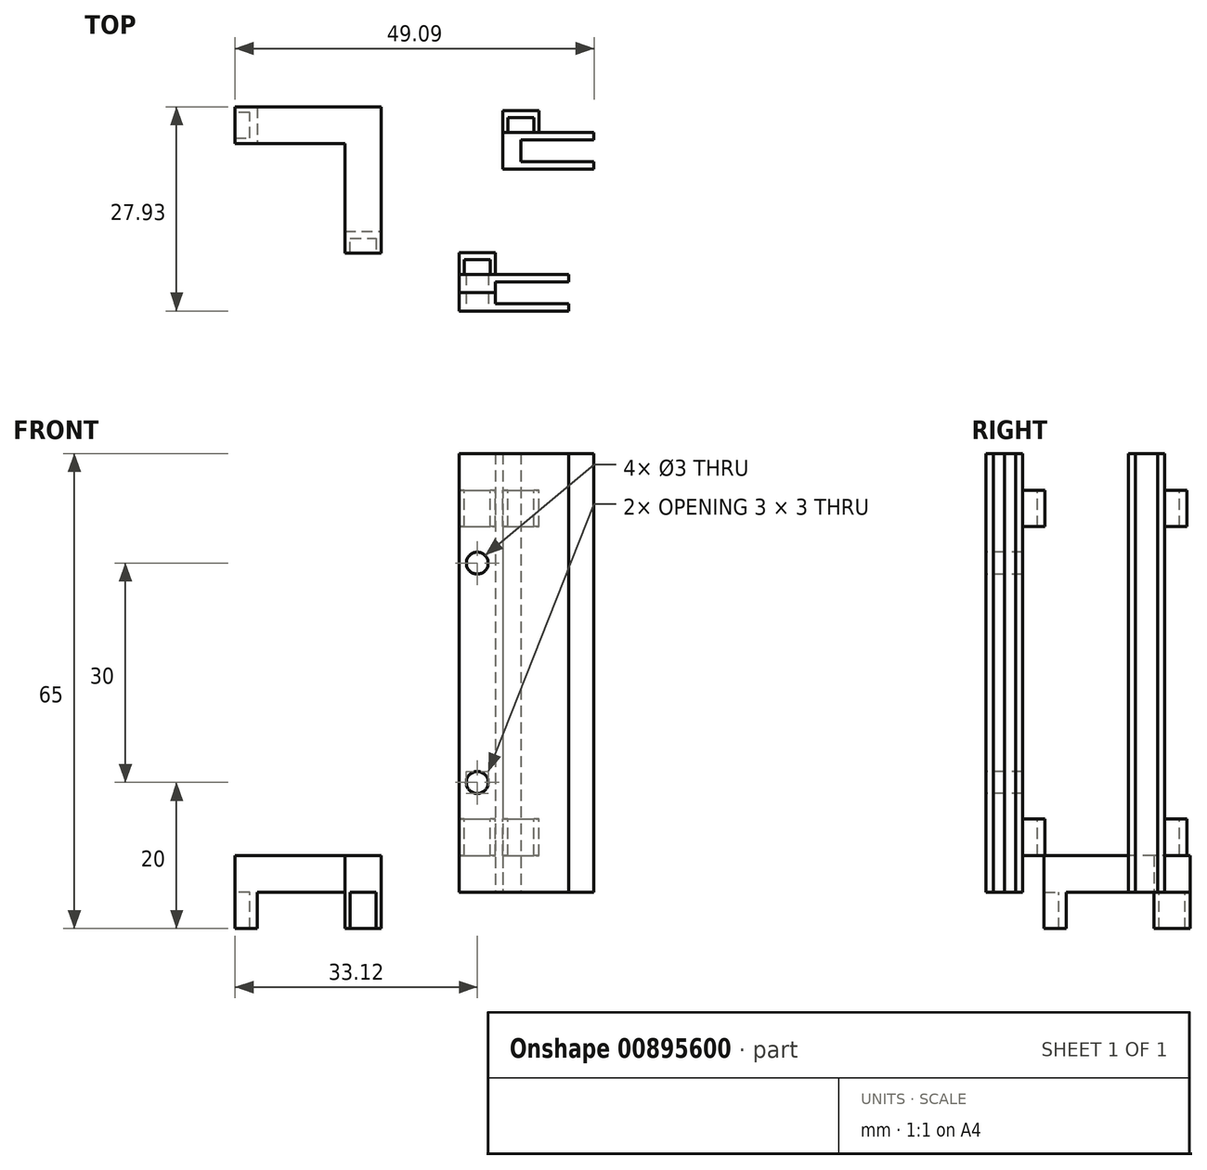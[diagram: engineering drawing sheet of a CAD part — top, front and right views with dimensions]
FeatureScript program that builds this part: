
annotation { "Feature Type Name" : "Feature", "Feature Type Description" : "" }
export const myFeature = defineFeature(function(context is Context, id is Id, definition is map)
    precondition{}
    {
        {
            var Q0;
            Q0=qCreatedBy(makeId("Top.planeOp"),FACE);
            var sketch = newSketch(context, id + "F0", { "sketchPlane" : qUnion([Q0])});
            skLineSegment(sketch, "E0.bottom", {"start": v(0, 0) * mm, "end": v(-10, 0) * mm});
            skLineSegment(sketch, "E0.top", {"start": v(0, 3) * mm, "end": v(-10, 3) * mm});
            skLineSegment(sketch, "E0.left", {"start": v(0, 0) * mm, "end": v(0, 3) * mm});
            skLineSegment(sketch, "E0.right", {"start": v(-10, 0) * mm, "end": v(-10, 3) * mm});
            skLineSegment(sketch, "E1.bottom", {"start": v(0, 0) * mm, "end": v(-15, 0) * mm});
            skLineSegment(sketch, "E1.top", {"start": v(0, -1) * mm, "end": v(-15, -1) * mm});
            skLineSegment(sketch, "E1.left", {"start": v(0, 0) * mm, "end": v(0, -1) * mm});
            skLineSegment(sketch, "E1.right", {"start": v(-15, 0) * mm, "end": v(-15, -1) * mm});
            skLineSegment(sketch, "E2.bottom", {"start": v(0, 3) * mm, "end": v(-15, 3) * mm});
            skLineSegment(sketch, "E2.top", {"start": v(0, 4) * mm, "end": v(-15, 4) * mm});
            skLineSegment(sketch, "E2.left", {"start": v(0, 3) * mm, "end": v(0, 4) * mm});
            skLineSegment(sketch, "E2.right", {"start": v(-15, 3) * mm, "end": v(-15, 4) * mm});
            skLineSegment(sketch, "E3", {"start": v(-15, 3) * mm, "end": v(-15, 0) * mm});
            skLineSegment(sketch, "E4", {"start": v(-15, 1.5) * mm, "end": v(-10, 1.5) * mm});
            skSolve(sketch);
        }
        {
            var Q0;
            Q0=makeQuery(id+"F0.imprint","IMPRINT",FACE,{"disambiguationData":[TD([[makeQuery(id+"F0.imprint","IMPRINT",EDGE,{"derivedFrom":sQuery(id+"F0.wireOp",EDGE,"E2.top")}),1.0]])]});
            var Q1;
            {var subQ3=sQuery(id+"F0.wireOp",EDGE,"E4");Q1=makeQuery(id+"F0.imprint","IMPRINT",FACE,{"disambiguationData":[TD([[makeQuery(id+"F0.imprint","IMPRINT",EDGE,{"derivedFrom":subQ3}),1.0]])]});}
            extrude(context, id + "F1", {"entities" : qUnion([Q0, Q1]), "depth" : 60 * mm});
        }
        {
            var Q0;
            {var subQ3=sQuery(id+"F0.wireOp",EDGE,"E4");Q0=makeQuery(id+"F0.imprint","IMPRINT",FACE,{"disambiguationData":[TD([[makeQuery(id+"F0.imprint","IMPRINT",EDGE,{"derivedFrom":subQ3}),-1.0]])]});}
            var Q1;
            Q1=makeQuery(id+"F0.imprint","IMPRINT",FACE,{"disambiguationData":[TD([[makeQuery(id+"F0.imprint","IMPRINT",EDGE,{"derivedFrom":sQuery(id+"F0.wireOp",EDGE,"E1.top")}),-1.0]])]});
            extrude(context, id + "F2", {"entities" : qUnion([Q0, Q1]), "depth" : 60 * mm});
        }
        {
            var Q0;
            Q0=makeQuery(id+"F2.opExtrude","SWEPT_FACE",FACE,{"disambiguationData":[OSD([sQuery(id+"F0.wireOp",EDGE,"E1.top")])]});
            var sketch = newSketch(context, id + "F3", { "sketchPlane" : qUnion([Q0])});
            skLineSegment(sketch, "E5.bottom", {"start": v(-15, 60) * mm, "end": v(-10, 60) * mm});
            skLineSegment(sketch, "E5.top", {"start": v(-15, 0) * mm, "end": v(-10, 0) * mm});
            skLineSegment(sketch, "E5.left", {"start": v(-15, 60) * mm, "end": v(-15, 0) * mm});
            skLineSegment(sketch, "E5.right", {"start": v(-10, 60) * mm, "end": v(-10, 0) * mm});
            skLineSegment(sketch, "E6.bottom", {"start": v(-15, 30) * mm, "end": v(-10, 30) * mm});
            skLineSegment(sketch, "E6.left", {"start": v(-15, 30) * mm, "end": v(-15, 60) * mm});
            skLineSegment(sketch, "E6.right", {"start": v(-10, 30) * mm, "end": v(-10, 60) * mm});
            skLineSegment(sketch, "E7.left", {"start": v(-15, 30) * mm, "end": v(-15, 0) * mm});
            skLineSegment(sketch, "E7.right", {"start": v(-10, 30) * mm, "end": v(-10, 0) * mm});
            skCircle(sketch, "E8", {"center": v(-12.5, 15) * mm, "radius": 1.5 * mm});
            skPoint(sketch, "E8.centerSnap0", {"position": v(-15, 15) * mm});
            skPoint(sketch, "E8.centerSnap1", {"position": v(-12.5, 30) * mm});
            skCircle(sketch, "E9", {"center": v(-12.5, 45) * mm, "radius": 1.5 * mm});
            skPoint(sketch, "E9.centerSnap0", {"position": v(-12.5, 60) * mm});
            skPoint(sketch, "E9.centerSnap1", {"position": v(-15, 45) * mm});
            skSolve(sketch);
        }
        {
            var Q0;
            Q0=sQuery(id+"F3.wireOp",VERTEX,"E9.center");
            var Q1;
            Q1=sQuery(id+"F3.wireOp",VERTEX,"E8.center");
            var Q2;
            Q2=makeQuery(id+"F1.opExtrude","SWEPT_BODY",BODY,{"disambiguationData":[OSD([sQuery(id+"F0.wireOp",EDGE,"E0.right"),sQuery(id+"F0.wireOp",EDGE,"E2.bottom"),sQuery(id+"F0.wireOp",EDGE,"E2.top"),sQuery(id+"F0.wireOp",EDGE,"E2.left"),sQuery(id+"F0.wireOp",EDGE,"E2.right"),sQuery(id+"F0.wireOp",EDGE,"E3"),sQuery(id+"F0.wireOp",EDGE,"E4")])]});
            var Q3;
            Q3=makeQuery(id+"F2.opExtrude","SWEPT_BODY",BODY,{"disambiguationData":[OSD([sQuery(id+"F0.wireOp",EDGE,"E0.right"),sQuery(id+"F0.wireOp",EDGE,"E1.bottom"),sQuery(id+"F0.wireOp",EDGE,"E1.top"),sQuery(id+"F0.wireOp",EDGE,"E1.left"),sQuery(id+"F0.wireOp",EDGE,"E1.right"),sQuery(id+"F0.wireOp",EDGE,"E3"),sQuery(id+"F0.wireOp",EDGE,"E4")])]});
            hole(context, id + "F4", {"style" : HoleStyle.SIMPLE, "endStyle" : HoleEndStyle.BLIND, "holeDiameter" : 3 * mm, "holeDepth" : 100 * mm, "tappedDepth" : 12 * mm, "tapClearance" : 3, "locations" : qUnion([Q0, Q1]), "scope" : qUnion([Q2, Q3])});
        }
        {
            var Q0;
            Q0=qCreatedBy(makeId("Top.planeOp"),FACE);
            var sketch = newSketch(context, id + "F5", { "sketchPlane" : qUnion([Q0])});
            skLineSegment(sketch, "E10.bottom", {"start": v(3.47, 22.43) * mm, "end": v(-6.53, 22.43) * mm});
            skLineSegment(sketch, "E10.top", {"start": v(3.47, 19.43) * mm, "end": v(-6.53, 19.43) * mm});
            skLineSegment(sketch, "E10.left", {"start": v(3.47, 22.43) * mm, "end": v(3.47, 19.43) * mm});
            skLineSegment(sketch, "E10.right", {"start": v(-6.53, 22.43) * mm, "end": v(-6.53, 19.43) * mm});
            skLineSegment(sketch, "E11.bottom", {"start": v(3.47, 20.93) * mm, "end": v(-9.03, 20.93) * mm});
            skLineSegment(sketch, "E11.top", {"start": v(3.47, 23.43) * mm, "end": v(-9.03, 23.43) * mm});
            skLineSegment(sketch, "E11.left", {"start": v(3.47, 20.93) * mm, "end": v(3.47, 23.43) * mm});
            skLineSegment(sketch, "E11.right", {"start": v(-9.03, 20.93) * mm, "end": v(-9.03, 23.43) * mm});
            skLineSegment(sketch, "E12.top", {"start": v(3.47, 18.43) * mm, "end": v(-9.03, 18.43) * mm});
            skLineSegment(sketch, "E12.left", {"start": v(3.47, 20.93) * mm, "end": v(3.47, 18.43) * mm});
            skLineSegment(sketch, "E12.right", {"start": v(-9.03, 20.93) * mm, "end": v(-9.03, 18.43) * mm});
            skSolve(sketch);
        }
        {
            var Q0;
            {var subQ1=sQuery(id+"F5.wireOp",EDGE,"E10.bottom");Q0=makeQuery(id+"F5.imprint","IMPRINT",FACE,{"disambiguationData":[TD([[makeQuery(id+"F5.imprint","IMPRINT",EDGE,{"derivedFrom":subQ1}),-1.0]])]});}
            var Q1;
            {var subQ5=sQuery(id+"F5.wireOp",EDGE,"E10.top");Q1=makeQuery(id+"F5.imprint","IMPRINT",FACE,{"disambiguationData":[TD([[makeQuery(id+"F5.imprint","IMPRINT",EDGE,{"derivedFrom":subQ5}),1.0]])]});}
            extrude(context, id + "F6", {"entities" : qUnion([Q0, Q1]), "depth" : 60 * mm});
        }
        {
            var Q0;
            Q0=makeQuery(id+"F1.opExtrude","CAP_FACE",FACE,{"disambiguationData":[OSD([sQuery(id+"F0.wireOp",EDGE,"E0.right"),sQuery(id+"F0.wireOp",EDGE,"E2.bottom"),sQuery(id+"F0.wireOp",EDGE,"E2.top"),sQuery(id+"F0.wireOp",EDGE,"E2.left"),sQuery(id+"F0.wireOp",EDGE,"E2.right"),sQuery(id+"F0.wireOp",EDGE,"E3"),sQuery(id+"F0.wireOp",EDGE,"E4")])],"isStart":false});
            var sketch = newSketch(context, id + "F7", { "sketchPlane" : qUnion([Q0])});
            skLineSegment(sketch, "E13", {"start": v(-15, 4) * mm, "end": v(-15, 7) * mm});
            skLineSegment(sketch, "E14", {"start": v(-15, 7) * mm, "end": v(-10, 7) * mm});
            skLineSegment(sketch, "E15", {"start": v(-10, 7) * mm, "end": v(-10, 4) * mm});
            skLineSegment(sketch, "E16", {"start": v(-10, 4) * mm, "end": v(-10.75, 4) * mm});
            skLineSegment(sketch, "E17", {"start": v(-15, 4) * mm, "end": v(-14.25, 4) * mm});
            skLineSegment(sketch, "E18", {"start": v(-14.25, 4) * mm, "end": v(-10.75, 4) * mm});
            skLineSegment(sketch, "E19", {"start": v(-10.75, 4) * mm, "end": v(-10.75, 6) * mm});
            skLineSegment(sketch, "E20", {"start": v(-14.25, 4) * mm, "end": v(-14.25, 6) * mm});
            skLineSegment(sketch, "E21", {"start": v(-14.25, 6) * mm, "end": v(-10.75, 6) * mm});
            skSolve(sketch);
        }
        {
            var Q0;
            Q0=makeQuery(id+"F7.imprint","IMPRINT",FACE,{"disambiguationData":[TD([[makeQuery(id+"F7.imprint","IMPRINT",EDGE,{"derivedFrom":sQuery(id+"F7.wireOp",EDGE,"E13")}),-1.0]])]});
            extrude(context, id + "F8", {"entities" : qUnion([Q0]), "operationType" : NewBodyOperationType.ADD, "oppositeDirection" : true, "depth" : 10 * mm, "hasSecondDirection" : true, "secondDirectionOppositeDirection" : true, "secondDirectionDepth" : 5 * mm});
        }
        {
            var Q0;
            Q0=makeQuery(id+"F7.imprint","IMPRINT",FACE,{"disambiguationData":[TD([[makeQuery(id+"F7.imprint","IMPRINT",EDGE,{"derivedFrom":sQuery(id+"F7.wireOp",EDGE,"E13")}),-1.0]])]});
            var Q1;
            Q1=makeQuery(id+"F1.opExtrude","CAP_FACE",FACE,{"disambiguationData":[OSD([sQuery(id+"F0.wireOp",EDGE,"E0.right"),sQuery(id+"F0.wireOp",EDGE,"E2.bottom"),sQuery(id+"F0.wireOp",EDGE,"E2.top"),sQuery(id+"F0.wireOp",EDGE,"E2.left"),sQuery(id+"F0.wireOp",EDGE,"E2.right"),sQuery(id+"F0.wireOp",EDGE,"E3"),sQuery(id+"F0.wireOp",EDGE,"E4")])],"isStart":true});
            extrude(context, id + "F9", {"entities" : qUnion([Q0]), "operationType" : NewBodyOperationType.ADD, "oppositeDirection" : true, "endBoundEntityFace" : qUnion([Q1]), "depth" : 55 * mm, "hasSecondDirection" : true, "secondDirectionOppositeDirection" : true, "secondDirectionDepth" : 50 * mm});
        }
        {
            var Q0;
            Q0=makeQuery(id+"F6.opExtrude","CAP_FACE",FACE,{"disambiguationData":[OSD([sQuery(id+"F5.wireOp",EDGE,"E10.bottom"),sQuery(id+"F5.wireOp",EDGE,"E10.top"),sQuery(id+"F5.wireOp",EDGE,"E10.right"),sQuery(id+"F5.wireOp",EDGE,"E11.top"),sQuery(id+"F5.wireOp",EDGE,"E11.left"),sQuery(id+"F5.wireOp",EDGE,"E11.right"),sQuery(id+"F5.wireOp",EDGE,"E12.top"),sQuery(id+"F5.wireOp",EDGE,"E12.left"),sQuery(id+"F5.wireOp",EDGE,"E12.right")])],"isStart":false});
            var sketch = newSketch(context, id + "F10", { "sketchPlane" : qUnion([Q0])});
            skLineSegment(sketch, "E22.bottom", {"start": v(-9.03, 23.43) * mm, "end": v(-4.03, 23.43) * mm});
            skLineSegment(sketch, "E22.top", {"start": v(-9.03, 26.43) * mm, "end": v(-4.03, 26.43) * mm});
            skLineSegment(sketch, "E22.left", {"start": v(-9.03, 23.43) * mm, "end": v(-9.03, 26.43) * mm});
            skLineSegment(sketch, "E22.right", {"start": v(-4.03, 23.43) * mm, "end": v(-4.03, 26.43) * mm});
            skLineSegment(sketch, "E23", {"start": v(-9.03, 23.43) * mm, "end": v(-8.28, 23.43) * mm});
            skLineSegment(sketch, "E24", {"start": v(-4.03, 23.43) * mm, "end": v(-4.78, 23.43) * mm});
            skLineSegment(sketch, "E25", {"start": v(-4.78, 23.43) * mm, "end": v(-8.28, 23.43) * mm});
            skLineSegment(sketch, "E26", {"start": v(-8.28, 23.43) * mm, "end": v(-8.28, 25.43) * mm});
            skLineSegment(sketch, "E27", {"start": v(-8.28, 25.43) * mm, "end": v(-4.78, 25.43) * mm});
            skLineSegment(sketch, "E28", {"start": v(-4.78, 25.43) * mm, "end": v(-4.78, 23.43) * mm});
            skSolve(sketch);
        }
        {
            var Q0;
            Q0=makeQuery(id+"F10.imprint","IMPRINT",FACE,{"disambiguationData":[TD([[makeQuery(id+"F10.imprint","IMPRINT",EDGE,{"derivedFrom":sQuery(id+"F10.wireOp",EDGE,"E22.top")}),-1.0]])]});
            extrude(context, id + "F11", {"entities" : qUnion([Q0]), "operationType" : NewBodyOperationType.ADD, "oppositeDirection" : true, "depth" : 10 * mm, "hasSecondDirection" : true, "secondDirectionOppositeDirection" : true, "secondDirectionDepth" : 5 * mm});
        }
        {
            var Q0;
            Q0=makeQuery(id+"F10.imprint","IMPRINT",FACE,{"disambiguationData":[TD([[makeQuery(id+"F10.imprint","IMPRINT",EDGE,{"derivedFrom":sQuery(id+"F10.wireOp",EDGE,"E22.top")}),-1.0]])]});
            extrude(context, id + "F12", {"entities" : qUnion([Q0]), "operationType" : NewBodyOperationType.ADD, "oppositeDirection" : true, "depth" : 55 * mm, "hasSecondDirection" : true, "secondDirectionOppositeDirection" : true, "secondDirectionDepth" : 50 * mm});
        }
        {
            var Q0;
            Q0=qCreatedBy(makeId("Top.planeOp"),FACE);
            var sketch = newSketch(context, id + "F13", { "sketchPlane" : qUnion([Q0])});
            skLineSegment(sketch, "E29.bottom", {"start": v(-30.62, 26.93) * mm, "end": v(-25.62, 26.93) * mm});
            skLineSegment(sketch, "E29.top", {"start": v(-30.62, 21.93) * mm, "end": v(-25.62, 21.93) * mm});
            skLineSegment(sketch, "E29.left", {"start": v(-30.62, 26.93) * mm, "end": v(-30.62, 21.93) * mm});
            skLineSegment(sketch, "E29.right", {"start": v(-25.62, 26.93) * mm, "end": v(-25.62, 21.93) * mm});
            skLineSegment(sketch, "E30.top", {"start": v(-30.62, 9.93) * mm, "end": v(-25.62, 9.93) * mm});
            skLineSegment(sketch, "E30.left", {"start": v(-30.62, 21.93) * mm, "end": v(-30.62, 9.93) * mm});
            skLineSegment(sketch, "E30.right", {"start": v(-25.62, 21.93) * mm, "end": v(-25.62, 9.93) * mm});
            skLineSegment(sketch, "E31.bottom", {"start": v(-30.62, 26.93) * mm, "end": v(-42.62, 26.93) * mm});
            skLineSegment(sketch, "E31.top", {"start": v(-30.62, 21.93) * mm, "end": v(-42.62, 21.93) * mm});
            skLineSegment(sketch, "E31.right", {"start": v(-42.62, 26.93) * mm, "end": v(-42.62, 21.93) * mm});
            skLineSegment(sketch, "E32.top", {"start": v(-30.62, 6.93) * mm, "end": v(-25.62, 6.93) * mm});
            skLineSegment(sketch, "E32.left", {"start": v(-30.62, 9.93) * mm, "end": v(-30.62, 6.93) * mm});
            skLineSegment(sketch, "E32.right", {"start": v(-25.62, 9.93) * mm, "end": v(-25.62, 6.93) * mm});
            skLineSegment(sketch, "E33.bottom", {"start": v(-42.62, 26.93) * mm, "end": v(-45.62, 26.93) * mm});
            skLineSegment(sketch, "E33.top", {"start": v(-42.62, 21.93) * mm, "end": v(-45.62, 21.93) * mm});
            skLineSegment(sketch, "E33.right", {"start": v(-45.62, 26.93) * mm, "end": v(-45.62, 21.93) * mm});
            skLineSegment(sketch, "E34", {"start": v(-45.62, 26.93) * mm, "end": v(-45.62, 26.18) * mm});
            skLineSegment(sketch, "E35", {"start": v(-45.62, 21.93) * mm, "end": v(-45.62, 22.68) * mm});
            skLineSegment(sketch, "E36", {"start": v(-45.62, 22.68) * mm, "end": v(-43.62, 22.68) * mm});
            skLineSegment(sketch, "E37", {"start": v(-43.62, 22.68) * mm, "end": v(-43.62, 26.18) * mm});
            skLineSegment(sketch, "E38", {"start": v(-43.62, 26.18) * mm, "end": v(-45.62, 26.18) * mm});
            skLineSegment(sketch, "E39", {"start": v(-30.62, 6.93) * mm, "end": v(-29.87, 6.93) * mm});
            skLineSegment(sketch, "E40", {"start": v(-29.87, 6.93) * mm, "end": v(-29.87, 8.93) * mm});
            skLineSegment(sketch, "E41", {"start": v(-29.87, 8.93) * mm, "end": v(-26.37, 8.93) * mm});
            skLineSegment(sketch, "E42", {"start": v(-26.37, 8.93) * mm, "end": v(-26.37, 6.93) * mm});
            skLineSegment(sketch, "E43", {"start": v(-26.37, 6.93) * mm, "end": v(-25.62, 6.93) * mm});
            skSolve(sketch);
        }
        {
            var Q0;
            Q0=qSketchRegion(id+"F13",true);
            extrude(context, id + "F14", {"entities" : qUnion([Q0]), "depth" : 5 * mm});
        }
        {
            var Q0;
            Q0=makeQuery(id+"F13.imprint","IMPRINT",FACE,{"disambiguationData":[TD([[makeQuery(id+"F13.imprint","IMPRINT",EDGE,{"derivedFrom":sQuery(id+"F13.wireOp",EDGE,"E32.top")}),1.0]])]});
            var Q1;
            Q1=makeQuery(id+"F13.imprint","IMPRINT",FACE,{"disambiguationData":[TD([[makeQuery(id+"F13.imprint","IMPRINT",EDGE,{"derivedFrom":sQuery(id+"F13.wireOp",EDGE,"E33.right")}),1.0]])]});
            extrude(context, id + "F15", {"entities" : qUnion([Q0, Q1]), "operationType" : NewBodyOperationType.ADD, "oppositeDirection" : true, "depth" : 5 * mm});
        }
    });
